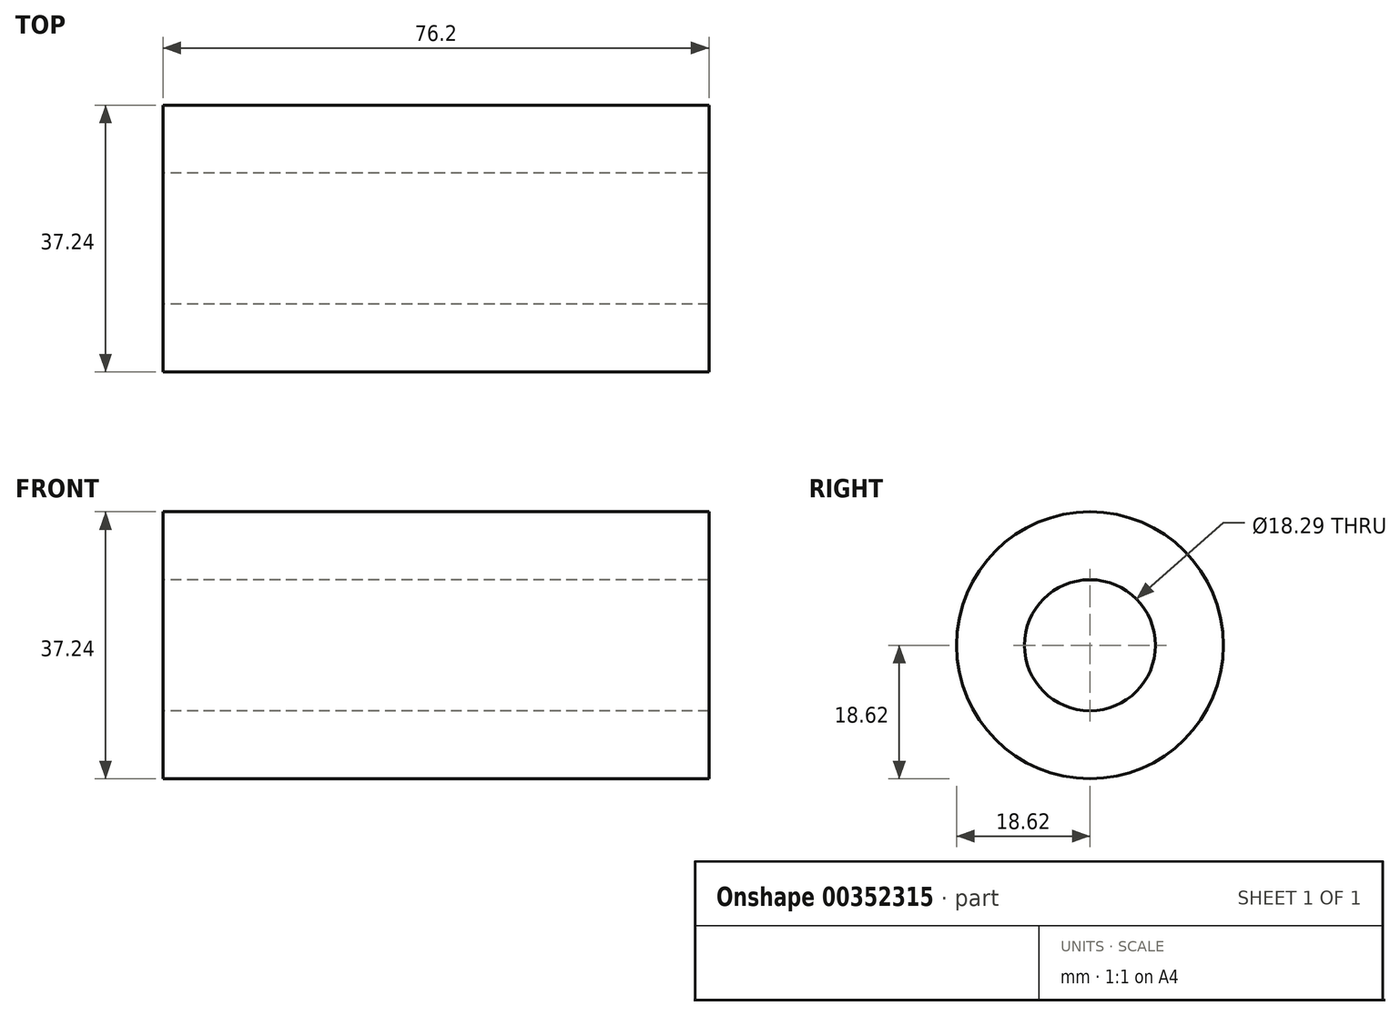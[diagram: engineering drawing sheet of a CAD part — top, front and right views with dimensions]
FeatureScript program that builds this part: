
annotation { "Feature Type Name" : "Feature", "Feature Type Description" : "" }
export const myFeature = defineFeature(function(context is Context, id is Id, definition is map)
    precondition{}
    {
        {
            var Q0;
            Q0=qCreatedBy(makeId("Right.planeOp"),FACE);
            var sketch = newSketch(context, id + "F0", { "sketchPlane" : qUnion([Q0])});
            skCircle(sketch, "E0", {"center": v(0, 0) * mm, "radius": 18.62 * mm});
            skSolve(sketch);
        }
        {
            var Q0;
            Q0=makeQuery(id+"F0.imprint","IMPRINT",FACE,{"disambiguationData":[TD([[makeQuery(id+"F0.imprint","IMPRINT",EDGE,{"derivedFrom":sQuery(id+"F0.wireOp",EDGE,"E0")}),1.0]])]});
            extrude(context, id + "F1", {"entities" : qUnion([Q0]), "depth" : 76.2 * mm});
        }
        {
            var Q0;
            Q0=qCreatedBy(makeId("Right.planeOp"),FACE);
            var sketch = newSketch(context, id + "F2", { "sketchPlane" : qUnion([Q0])});
            skCircle(sketch, "E1", {"center": v(0, 0) * mm, "radius": 9.14 * mm});
            skSolve(sketch);
        }
        {
            var Q0;
            Q0=makeQuery(id+"F2.imprint","IMPRINT",FACE,{"disambiguationData":[TD([[makeQuery(id+"F2.imprint","IMPRINT",EDGE,{"derivedFrom":sQuery(id+"F2.wireOp",EDGE,"E1")}),1.0]])]});
            extrude(context, id + "F3", {"entities" : qUnion([Q0]), "operationType" : NewBodyOperationType.REMOVE, "depth" : 76.2 * mm});
        }
    });
